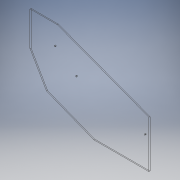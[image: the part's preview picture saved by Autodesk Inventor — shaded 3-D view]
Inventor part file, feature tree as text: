
AUTODESK INVENTOR PART (.ipt)
format: ipt  version: 2018.2 (Build 222227000, 227)  size: 135,680 bytes
history: native  units: mm
features: other x4, reference x4, extrude x3, sketch x3, chamfer x1
ambient origin geometry x8: Origin, YZ Plane, XZ Plane, XY Plane, X Axis, Y Axis, Z Axis, Center Point
bodies: Body1 (feature_tree)
feature tree (15):
  other  "ソリッド1"
  extrude  "押し出し1"  Depth=555.0mm
  extrude  "押し出し4"  Depth=555.0mm
  extrude  "押し出し5"  Depth=5.0mm TaperAngle=0.0deg
  chamfer  "面取り2"  Distance=5.0mm
  sketch  "スケッチ1"
  sketch  "スケッチ3"
  sketch  "スケッチ5"
  reference  "参照1"
  reference  "参照2"
  reference  "参照3"
  reference  "参照4"
  other  "<userpath>\Documents\Inventor\AeroCAD2018\設計\Rr.wing\model.iam"
  other  "model.iam"
  other  "endplate:1"
